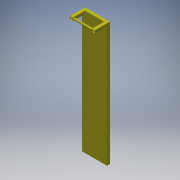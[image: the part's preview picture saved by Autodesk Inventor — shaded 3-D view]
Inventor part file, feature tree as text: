
AUTODESK INVENTOR PART (.ipt)
format: ipt  version: 2017 SP1 (Build 210196100, 196)  size: 143,360 bytes
history: native  units: in
note: dims shown in document units (in); Inventor stores cm internally (conversion verified against a paired STEP export)
features: extrude x3, sketch x3
ambient origin geometry x8: Origin, YZ Plane, XZ Plane, XY Plane, X Axis, Y Axis, Z Axis, Center Point
bodies: Solid1 (feature_tree)
feature tree (6):
  extrude  "Extrusion1"  Depth=2.0in
  extrude  "Extrusion2"  Depth=0.125in
  extrude  "Extrusion3"  Depth=84.375in
  sketch  "Sketch1"  dims[d0=13.0in d1=2.0in]
  sketch  "Sketch2"  dims[d2=0.125in d3=0.125in]
  sketch  "Sketch3"  dims[d4=8.25in d5=0.0in d6=1.25in d7=0.75in d8=0.125in d9=8.25in d10=0.0in d11=17.0in d12=2.0in d13=84.375in d14=0.0in]
